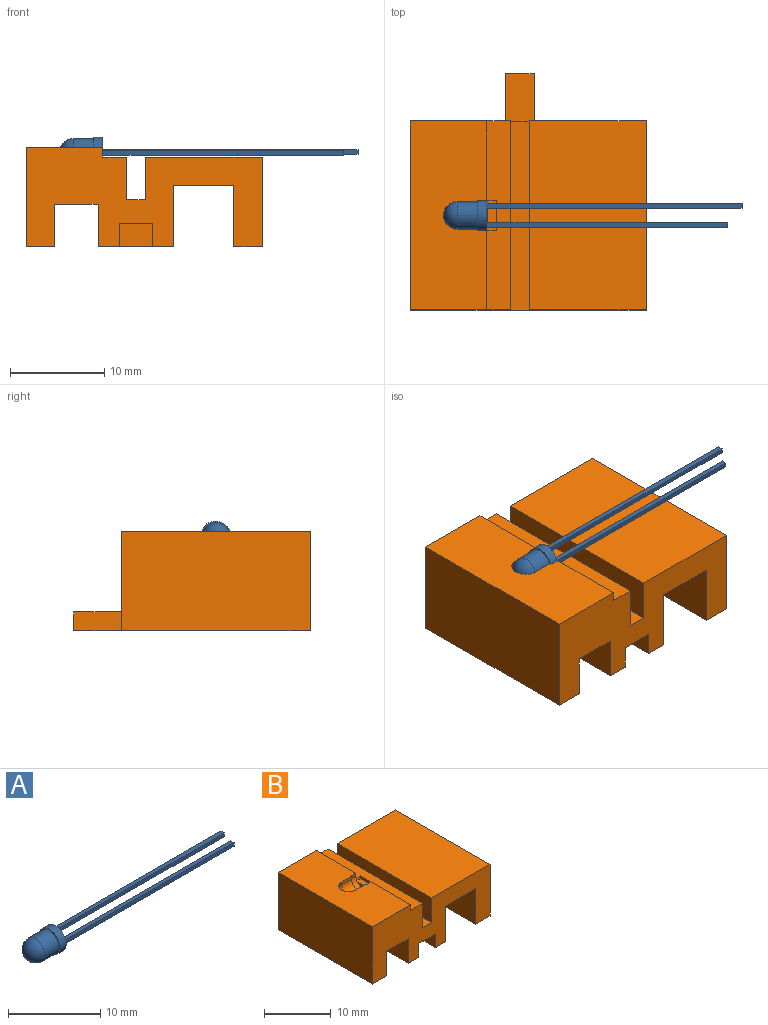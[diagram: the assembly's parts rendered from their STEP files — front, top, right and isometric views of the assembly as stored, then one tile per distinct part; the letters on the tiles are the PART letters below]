
ASSEMBLY  parts=2 mates=1
PART A: 15 faces, bbox 31.6x3.2x3.2 mm
  f0: plane 25.5x0.5mm, normal (0,0,1), area 12.8mm2, adj f1,f3,f4,f14
  f1: plane 25.5x0.5mm, normal (0,-1,0), area 12.8mm2, adj f0,f2,f4,f14
  f2: plane 25.5x0.5mm, normal (0,0,-1), area 12.8mm2, adj f1,f3,f4,f14
  f3: plane 25.5x0.5mm, normal (0,1,0), area 12.8mm2, adj f0,f2,f4,f14
  f4: plane 3.2x3.2mm, normal (1,0,0), area 7.5mm2, adj f0,f1,f2,f3,f6,f9,f10,f11
  f5: sphere r=1.45mm, area 13.2mm2, adj f8
  f6: cylinder r=1.6mm len=3.2mm, axis (-1,0,0), area 10.1mm2, adj f4,f7
  f7: plane 3.2x3.2mm, normal (-1,0,0), area 1.4mm2, adj f6,f8
  f8: cylinder r=1.45mm len=2.9mm, axis (-1,0,0), area 19.6mm2, adj f5,f7
  f9: plane 27x0.5mm, normal (0,0,-1), area 13.5mm2, adj f4,f10,f12,f13
  f10: plane 27x0.5mm, normal (0,1,0), area 13.5mm2, adj f4,f9,f11,f13
  f11: plane 27x0.5mm, normal (0,0,1), area 13.5mm2, adj f4,f10,f12,f13
  f12: plane 27x0.5mm, normal (0,-1,0), area 13.5mm2, adj f4,f9,f11,f13
  f13: plane 0.5x0.5mm, normal (1,0,0), area 0.3mm2, adj f9,f10,f11,f12
  f14: plane 0.5x0.5mm, normal (1,0,0), area 0.3mm2, adj f0,f1,f2,f3
PART B: 43 faces, bbox 25x25x10.5 mm
  f0: plane 3.25x0.5mm, normal (-1,0,0), area 1.6mm2, adj f2,f20,f33,f34
  f1: plane 8.72x1.5mm, normal (1,0,0), area 8.5mm2, adj f2,f7,f15,f20,f25,f26,f34
  f2: plane 3.25x1mm, normal (0,0,1), area 3mm2, adj f0,f1,f3,f11,f15,f33,f34
  f3: plane 8.72x1.5mm, normal (1,0,0), area 8.5mm2, adj f2,f6,f15,f20,f21,f26,f33
  f4: plane 25x8mm, normal (0,0,-1), area 157.5mm2, adj f6,f7,f29,f30,f35,f37,f38,f39
  f5: plane 20x3mm, normal (0,0,-1), area 60mm2, adj f6,f7,f9,f27
  f6: plane 25x10.5mm, normal (0,-1,0), area 165.6mm2, adj f3,f4,f5,f8,f9,f10,f16,f17
  f7: plane 25x10.5mm, normal (0,1,0), area 168.4mm2, adj f1,f4,f5,f8,f9,f10,f16,f17
  f8: plane 20x10.5mm, normal (-1,0,0), area 210mm2, adj f6,f7,f10,f26
  f9: plane 20x9.5mm, normal (1,0,0), area 190mm2, adj f5,f6,f7,f19
  f10: plane 20x3mm, normal (0,0,-1), area 60mm2, adj f6,f7,f8,f32
  f11: plane 2.56x0.63mm, normal (-1,0,0), area 1.1mm2, adj f2,f15
  f12: sphere r=1.47mm, area 6.8mm2, adj f13,f23
  f13: cylinder r=1.47mm len=2.95mm, axis (-1,0,0), area 9.8mm2, adj f12,f14,f22,f24
  f14: plane 3.25x2.13mm, normal (1,0,0), area 0.9mm2, adj f13,f15,f21,f22,f24,f25,f26
  f15: cylinder r=1.62mm len=3.25mm, axis (-1,0,0), area 5.4mm2, adj f1,f2,f3,f11,f14,f21,f25
  f16: plane 20x4.5mm, normal (1,0,0), area 90mm2, adj f6,f7,f17,f20
  f17: plane 20x2mm, normal (0,0,1), area 40mm2, adj f6,f7,f16,f18
  f18: plane 20x4.5mm, normal (-1,0,0), area 90mm2, adj f6,f7,f17,f19
  f19: plane 20x12.37mm, normal (0,0,1), area 247.4mm2, adj f6,f7,f9,f18
  f20: plane 20x2.5mm, normal (0,0,1), area 46.8mm2, adj f0,f1,f3,f6,f7,f16,f33,f34
  f21: plane 1.01x0.5mm, normal (0,1,0), area 0.5mm2, adj f3,f14,f15,f26
  f22: plane 2.13x0.5mm, normal (0,1,0), area 1.1mm2, adj f13,f14,f23,f26
  f23: cylinder r=1.47mm len=2.95mm, axis (0,0,-1), area 2.3mm2, adj f12,f22,f24,f26
  f24: plane 2.13x0.5mm, normal (0,-1,0), area 1.1mm2, adj f13,f14,f23,f26
  f25: plane 1.01x0.5mm, normal (0,-1,0), area 0.5mm2, adj f1,f14,f15,f26
  f26: plane 20x8.13mm, normal (0,0,1), area 149.6mm2, adj f1,f3,f6,f7,f8,f14,f21,f22
  f27: plane 20x6.5mm, normal (-1,0,0), area 130mm2, adj f5,f6,f7,f28
  f28: plane 20x6.37mm, normal (0,0,-1), area 127.4mm2, adj f6,f7,f27,f29
  f29: plane 20x6.5mm, normal (1,0,0), area 130mm2, adj f4,f6,f7,f28
  f30: plane 20x4.5mm, normal (-1,0,0), area 90mm2, adj f4,f6,f7,f31
  f31: plane 20x4.63mm, normal (0,0,-1), area 92.6mm2, adj f6,f7,f30,f32
  f32: plane 20x4.5mm, normal (1,0,0), area 90mm2, adj f6,f7,f10,f31
  f33: plane 1x0.5mm, normal (0,1,0), area 0.5mm2, adj f0,f2,f3,f20
  f34: plane 1x0.5mm, normal (0,-1,0), area 0.5mm2, adj f0,f1,f2,f20
  f35: plane 5x2.5mm, normal (-1,0,0), area 12.5mm2, adj f4,f6,f36,f38
  f36: plane 5x3.5mm, normal (0,0,-1), area 17.5mm2, adj f6,f35,f37,f38
  f37: plane 5x2.5mm, normal (1,0,0), area 12.5mm2, adj f4,f6,f36,f38
  f38: plane 3.5x2.5mm, normal (0,-1,0), area 8.8mm2, adj f4,f35,f36,f37
  f39: plane 5x2mm, normal (-1,0,0), area 10mm2, adj f4,f7,f40,f42
  f40: plane 5x3mm, normal (0,0,1), area 15mm2, adj f7,f39,f41,f42
  f41: plane 5x2mm, normal (1,0,0), area 10mm2, adj f4,f7,f40,f42
  f42: plane 3x2mm, normal (0,1,0), area 6mm2, adj f4,f39,f40,f41
PLACE A rot(axis=(1,0,0),92deg) t=(-3.99,0.47,4.55)mm
PLACE B t=(-3.98,0.47,4.55)mm fixed
MATE cylindrical A.f6 <-> B.f13  axis (-1,0,0) through (-2.91,0.47,4.55)mm
